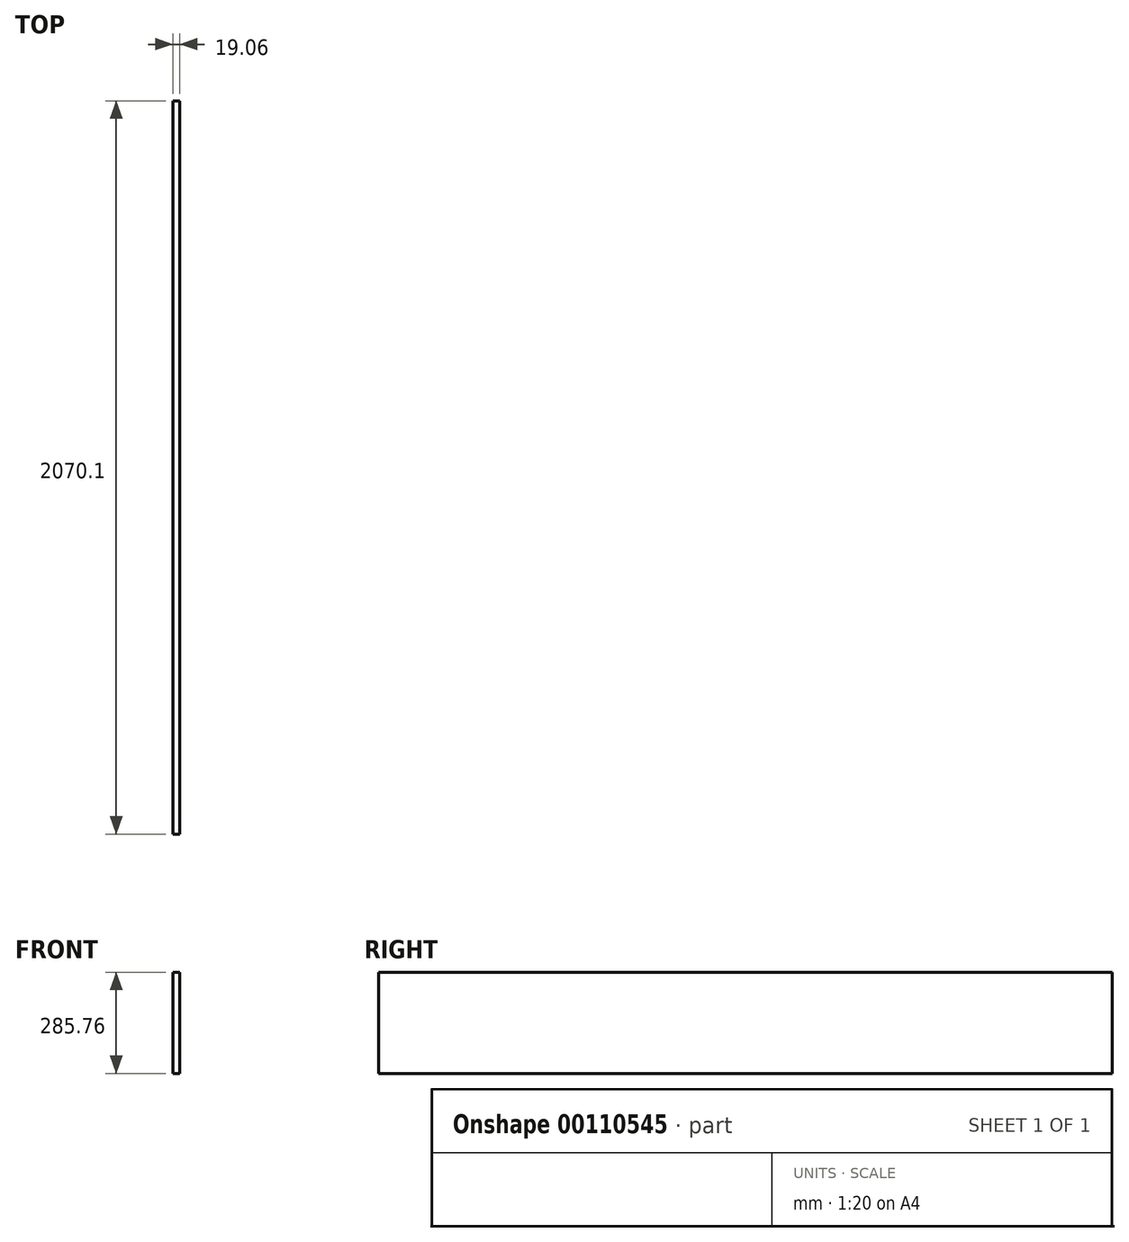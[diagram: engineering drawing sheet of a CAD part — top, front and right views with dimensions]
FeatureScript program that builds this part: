
annotation { "Feature Type Name" : "Feature", "Feature Type Description" : "" }
export const myFeature = defineFeature(function(context is Context, id is Id, definition is map)
    precondition{}
    {
        {
            var Q0;
            Q0=qCreatedBy(makeId("Front.planeOp"),FACE);
            var sketch = newSketch(context, id + "F0", { "sketchPlane" : qUnion([Q0])});
            skLineSegment(sketch, "E0.bottom", {"start": v(9.53, 142.88) * mm, "end": v(-9.52, 142.88) * mm});
            skLineSegment(sketch, "E0.top", {"start": v(9.53, -142.88) * mm, "end": v(-9.52, -142.88) * mm});
            skLineSegment(sketch, "E0.left", {"start": v(9.53, 142.88) * mm, "end": v(9.53, -142.88) * mm});
            skLineSegment(sketch, "E0.right", {"start": v(-9.52, 142.88) * mm, "end": v(-9.52, -142.88) * mm});
            skPoint(sketch, "E0.middle", {"position": v(0, 0) * mm});
            skSolve(sketch);
        }
        {
            var Q0;
            Q0=makeQuery(id+"F0.imprint","IMPRINT",FACE,{"disambiguationData":[TD([[makeQuery(id+"F0.imprint","IMPRINT",EDGE,{"derivedFrom":sQuery(id+"F0.wireOp",EDGE,"E0.bottom")}),1.0]])]});
            extrude(context, id + "F1", {"entities" : qUnion([Q0]), "endBound" : BoundingType.SYMMETRIC, "depth" : 2070.1 * mm});
        }
    });
